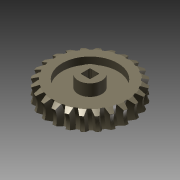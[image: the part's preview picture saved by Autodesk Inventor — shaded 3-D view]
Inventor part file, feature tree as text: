
AUTODESK INVENTOR PART (.ipt)
format: ipt  version: 2013 (Build 170138000, 138)  size: 680,960 bytes
history: native  units: mm (DEFAULTED — no unit token found)
features: other x10, sketch x5, plane x3, extrude x3, pattern_circular x1, mirror x1
ambient origin geometry x5: Origin, X Axis, Y Axis, Z Axis, Center Point
bodies: Solid1 (feature_tree)
feature tree (23):
  other  "Tooth Plane"
  other  "Base Body Sketch"
  other  "Base Body"
  other  "Base Body2"
  plane  "Work Plane13"
  other  "Tooth"
  pattern_circular  "Tooth Pattern"  [2 undecoded]
  plane  "Work Plane14"
  plane  "Work Plane15"
  extrude  "Extrusion1"  Depth=0.9525mm
  extrude  "Extrusion2"  TaperAngle=90.0deg  [1 undecoded]
  mirror  "Mirror1"
  other  "iFeature2:1"
  other  "Tooth Sketch"
  sketch  "Sketch8"  dims[d35=90.0deg]
  other  "Srf1"
  sketch  "Sketch9"  dims[d37=-0.7983mm]
  sketch  "Sketch10"  dims[d38=19.05mm]
  sketch  "Sketch11"  dims[d39=3.490659mm]
  sketch  "Sketch12"  dims[d40=5.103701mm d41=6.316462mm d42=0.9525mm d43=90.0deg d44=240.0mm d46=360.0deg d50=4.481768mm d75=1.308997mm d77=24.255213mm d78=6.35mm d79=0.0mm d83=1.308997mm d85=180.0deg d87=28.498978mm d89=10.611656mm d90=90.0deg d92=6.35mm d93=19.05mm d94=18.796mm d95=2.3876mm d96=0.0mm d97=8.001mm d98=3.9878mm d99=0.0mm d100=25.4mm d101=0.0mm d102=0.0mm d103=0.0mm]
  other  "Srf2"
  other  "Pitch Diameter"
  extrude  "ExtrusionSrf2"  Depth=240.0mm
note: 3 required parameter values undecoded (feature->parameter linkage not recoverable at this tier; creation-order binding heuristic only, values carry confidence <= 0.55)
